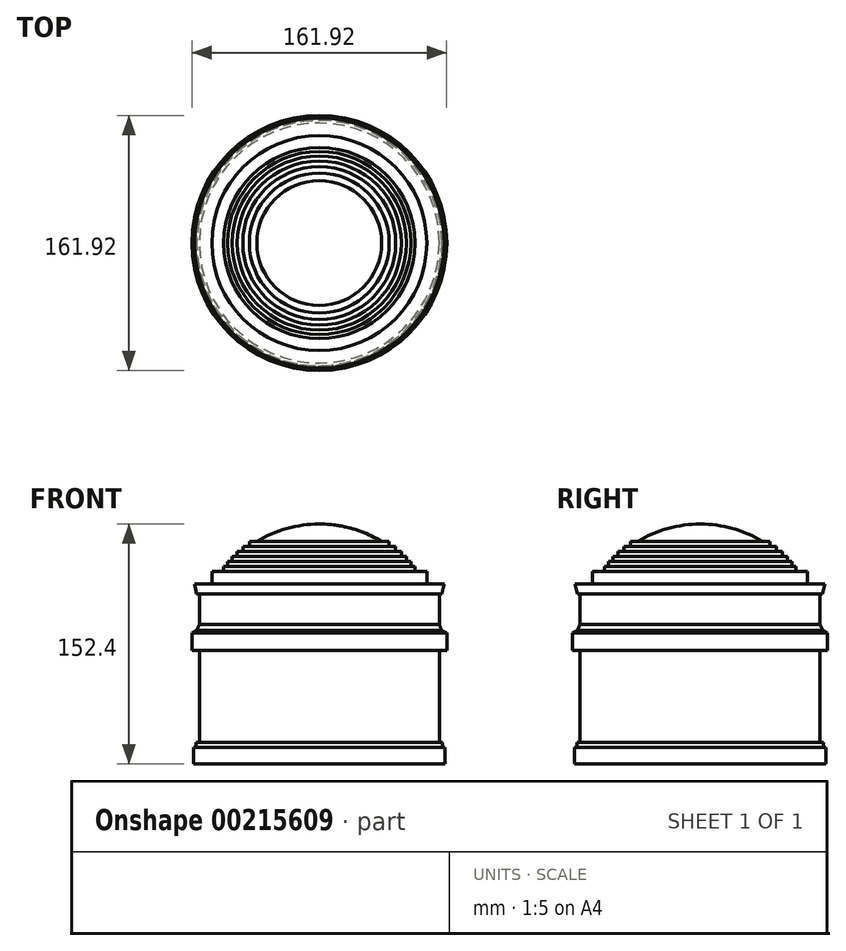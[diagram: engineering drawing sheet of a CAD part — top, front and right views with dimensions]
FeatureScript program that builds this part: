
annotation { "Feature Type Name" : "Feature", "Feature Type Description" : "" }
export const myFeature = defineFeature(function(context is Context, id is Id, definition is map)
    precondition{}
    {
        {
            var Q0;
            Q0=qCreatedBy(makeId("Front.planeOp"),FACE);
            var sketch = newSketch(context, id + "F0", { "sketchPlane" : qUnion([Q0])});
            skArc(sketch, "E0", {"start": v(0, -76.2) * mm, "mid": v(76.2, 0) * mm, "end": v(0, 76.2) * mm, "construction": true});
            skLineSegment(sketch, "E1.bottom", {"start": v(0, 38.1) * mm, "end": v(76.2, 38.1) * mm, "construction": true});
            skLineSegment(sketch, "E1.top", {"start": v(0, -76.2) * mm, "end": v(76.2, -76.2) * mm, "construction": true});
            skLineSegment(sketch, "E1.left", {"start": v(0, 38.1) * mm, "end": v(0, -76.2) * mm});
            skLineSegment(sketch, "E1.right", {"start": v(76.2, 38.1) * mm, "end": v(76.2, -76.2) * mm, "construction": true});
            skLineSegment(sketch, "E2", {"start": v(0, 0) * mm, "end": v(0, 76.2) * mm, "construction": true});
            skPoint(sketch, "E3", {"position": v(0, 38.1) * mm});
            skLineSegment(sketch, "E4", {"start": v(0, -76.2) * mm, "end": v(79.87, -76.2) * mm});
            skLineSegment(sketch, "E5", {"start": v(79.87, -76.2) * mm, "end": v(79.87, -65.78) * mm});
            skLineSegment(sketch, "E6", {"start": v(79.87, -65.78) * mm, "end": v(78.25, -65.78) * mm});
            skLineSegment(sketch, "E7", {"start": v(78.25, -65.78) * mm, "end": v(78.25, -62.5) * mm});
            skLineSegment(sketch, "E8", {"start": v(78.25, -62.5) * mm, "end": v(76.2, -62.5) * mm});
            skLineSegment(sketch, "E9", {"start": v(76.2, -62.5) * mm, "end": v(76.2, -4.2) * mm});
            skLineSegment(sketch, "E10", {"start": v(76.2, -4.2) * mm, "end": v(80.96, -4.2) * mm});
            skLineSegment(sketch, "E11", {"start": v(80.96, -4.2) * mm, "end": v(80.96, 6.91) * mm});
            skLineSegment(sketch, "E12", {"start": v(80.96, 6.91) * mm, "end": v(77.84, 8.49) * mm});
            skLineSegment(sketch, "E13", {"start": v(77.84, 8.49) * mm, "end": v(76.2, 12.35) * mm});
            skLineSegment(sketch, "E14", {"start": v(76.2, 12.35) * mm, "end": v(76.2, 31.75) * mm});
            skLineSegment(sketch, "E15", {"start": v(76.2, 31.75) * mm, "end": v(77.79, 31.75) * mm});
            skLineSegment(sketch, "E16", {"start": v(77.79, 31.75) * mm, "end": v(79.37, 38.1) * mm});
            skLineSegment(sketch, "E17", {"start": v(79.37, 38.1) * mm, "end": v(68.26, 38.1) * mm});
            skLineSegment(sketch, "E18", {"start": v(68.26, 38.1) * mm, "end": v(68.26, 46.04) * mm});
            skLineSegment(sketch, "E19", {"start": v(68.26, 46.04) * mm, "end": v(60.72, 46.04) * mm});
            skLineSegment(sketch, "E20", {"start": v(60.72, 46.04) * mm, "end": v(60.72, 49.21) * mm});
            skLineSegment(sketch, "E21", {"start": v(60.72, 49.21) * mm, "end": v(58.18, 49.21) * mm});
            skLineSegment(sketch, "E22", {"start": v(58.18, 49.21) * mm, "end": v(58.18, 52.39) * mm});
            skLineSegment(sketch, "E23", {"start": v(58.18, 52.39) * mm, "end": v(55.34, 52.39) * mm});
            skLineSegment(sketch, "E24", {"start": v(55.34, 52.39) * mm, "end": v(55.34, 55.56) * mm});
            skLineSegment(sketch, "E25", {"start": v(55.34, 55.56) * mm, "end": v(52.15, 55.56) * mm});
            skLineSegment(sketch, "E26", {"start": v(52.15, 55.56) * mm, "end": v(52.15, 58.74) * mm});
            skLineSegment(sketch, "E27", {"start": v(52.15, 58.74) * mm, "end": v(48.54, 58.74) * mm});
            skLineSegment(sketch, "E28", {"start": v(48.54, 58.74) * mm, "end": v(48.54, 61.91) * mm});
            skLineSegment(sketch, "E29", {"start": v(48.54, 61.91) * mm, "end": v(44.42, 61.91) * mm});
            skLineSegment(sketch, "E30", {"start": v(44.42, 61.91) * mm, "end": v(44.42, 65.09) * mm});
            skLineSegment(sketch, "E31", {"start": v(44.42, 65.09) * mm, "end": v(39.62, 65.09) * mm});
            skArc(sketch, "E32", {"start": v(39.62, 65.09) * mm, "mid": v(20.58, 73.37) * mm, "end": v(0, 76.2) * mm});
            skLineSegment(sketch, "E33", {"start": v(0, 76.2) * mm, "end": v(0, 38.1) * mm});
            skSolve(sketch);
        }
        {
            var Q0;
            Q0=makeQuery(id+"F0.imprint","IMPRINT",FACE,{"disambiguationData":[TD([[makeQuery(id+"F0.imprint","IMPRINT",EDGE,{"derivedFrom":sQuery(id+"F0.wireOp",EDGE,"E1.left")}),1.0]])]});
            var Q1;
            Q1=sQuery(id+"F0.wireOp",EDGE,"E1.left");
            revolve(context, id + "F1", {"entities" : qUnion([Q0]), "axis" : qUnion([Q1]), "revolveType" : RevolveType.FULL});
        }
    });
